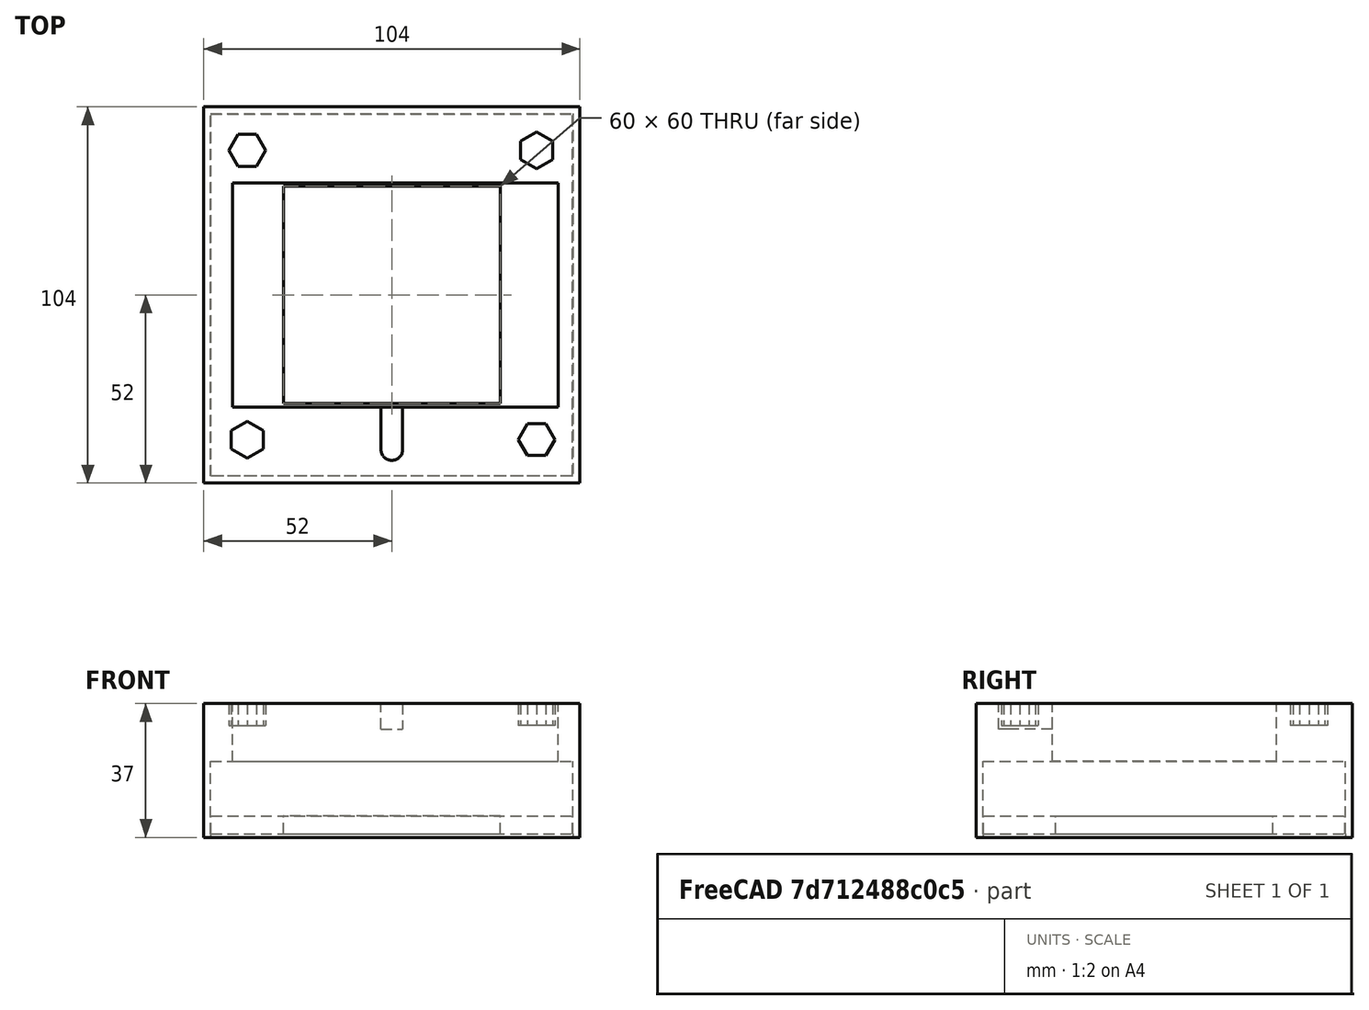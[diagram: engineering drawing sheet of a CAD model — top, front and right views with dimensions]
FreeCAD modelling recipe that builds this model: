
FCSTD DOCUMENT  (FreeCAD 1.0R39319 (Git))
Label: matrix-3-box-step
License: All rights reserved
LicenseURL: https://en.wikipedia.org/wiki/All_rights_reserved
objects: Part::Box×3, Part::Cut×2, Part::Feature×1
note: 6 computed .brp shape members not serialized (recipe doc carries the construction recipe); baked Part::Feature solids carry a one-line shape summary decoded from their .brp

FEATURE [Part::Feature] Part__Feature  label="Box"
  shape: bbox 104 x 104 x 37 mm, 80 faces (baked)
FEATURE [Part::Box] Box  label="Cube"
  AttacherType = Attacher::AttachEngine3D
  Height = 5
  Length = 100
  Placement = pos=(-50,-50,0) rot=(0,0,1;0rad)
  Width = 100
FEATURE [Part::Box] Box001  label="Cube001"
  AttacherType = Attacher::AttachEngine3D
  Height = 10
  Length = 60
  Placement = pos=(-30,-30,0) rot=(0,0,1;0rad)
  Width = 60
FEATURE [Part::Cut] Cut
  Base = -> Box
  Tool = -> Box001
FEATURE [Part::Box] Box002  label="Cube002"
  AttacherType = Attacher::AttachEngine3D
  Height = 20
  Length = 90
  Placement = pos=(-44,-31,17) rot=(0,0,1;0rad)
  Width = 62
FEATURE [Part::Cut] Cut001
  Base = -> Part__Feature
  Tool = -> Box002
